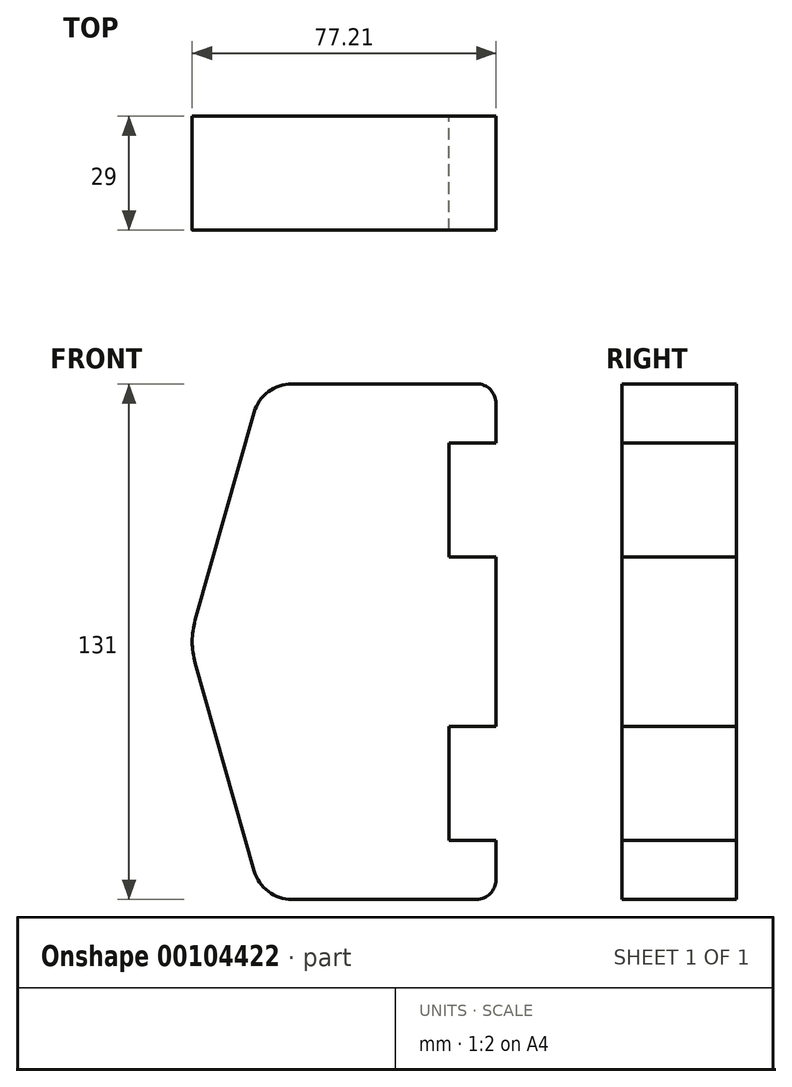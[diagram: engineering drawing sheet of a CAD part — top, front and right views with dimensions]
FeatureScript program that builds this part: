
annotation { "Feature Type Name" : "Feature", "Feature Type Description" : "" }
export const myFeature = defineFeature(function(context is Context, id is Id, definition is map)
    precondition{}
    {
        {
            var Q0;
            Q0=qCreatedBy(makeId("Front.planeOp"),FACE);
            var sketch = newSketch(context, id + "F0", { "sketchPlane" : qUnion([Q0])});
            skLineSegment(sketch, "E0", {"start": v(0, 0) * mm, "end": v(0, 21.5) * mm});
            skLineSegment(sketch, "E1", {"start": v(0, 21.5) * mm, "end": v(-12, 21.5) * mm});
            skLineSegment(sketch, "E2", {"start": v(-12, 21.5) * mm, "end": v(-12, 50.5) * mm});
            skLineSegment(sketch, "E3", {"start": v(-12, 50.5) * mm, "end": v(0, 50.5) * mm});
            skLineSegment(sketch, "E4", {"start": v(0, 50.5) * mm, "end": v(0, 60.5) * mm});
            skLineSegment(sketch, "E5", {"start": v(-5, 65.5) * mm, "end": v(-51.84, 65.5) * mm});
            skLineSegment(sketch, "E6", {"start": v(-61.46, 58.23) * mm, "end": v(-76.45, 5.46) * mm});
            skLineSegment(sketch, "E7", {"start": v(36.06, 0) * mm, "end": v(-91.54, 0) * mm, "construction": true});
            skLineSegment(sketch, "E8.MirrorCS", {"start": v(-61.46, -58.23) * mm, "end": v(-76.45, -5.46) * mm});
            skLineSegment(sketch, "E9.MirrorCS", {"start": v(-5, -65.5) * mm, "end": v(-51.84, -65.5) * mm});
            skLineSegment(sketch, "E10.MirrorCS", {"start": v(0, -50.5) * mm, "end": v(0, -60.5) * mm});
            skLineSegment(sketch, "E11.MirrorCS", {"start": v(-12, -50.5) * mm, "end": v(0, -50.5) * mm});
            skLineSegment(sketch, "E12.MirrorCS", {"start": v(-12, -21.5) * mm, "end": v(-12, -50.5) * mm});
            skLineSegment(sketch, "E13.MirrorCS", {"start": v(0, -21.5) * mm, "end": v(-12, -21.5) * mm});
            skLineSegment(sketch, "E14.MirrorCS", {"start": v(0, 0) * mm, "end": v(0, -21.5) * mm});
            skPoint(sketch, "E15.visualSharp", {"position": v(-59.4, 65.5) * mm});
            skArc(sketch, "E15.filletArc", {"start": v(-51.84, 65.5) * mm, "mid": v(-57.87, 63.48) * mm, "end": v(-61.46, 58.23) * mm});
            skPoint(sketch, "E16.visualSharp", {"position": v(0, 65.5) * mm});
            skArc(sketch, "E16.filletArc", {"start": v(0, 60.5) * mm, "mid": v(-1.46, 64.04) * mm, "end": v(-5, 65.5) * mm});
            skPoint(sketch, "E17.visualSharp", {"position": v(-78, 0) * mm});
            skArc(sketch, "E17.filletArc", {"start": v(-76.45, 5.46) * mm, "mid": v(-77.2, 0) * mm, "end": v(-76.45, -5.46) * mm});
            skPoint(sketch, "E18.visualSharp", {"position": v(-59.4, -65.5) * mm});
            skArc(sketch, "E18.filletArc", {"start": v(-61.46, -58.23) * mm, "mid": v(-57.87, -63.48) * mm, "end": v(-51.84, -65.5) * mm});
            skPoint(sketch, "E19.visualSharp", {"position": v(0, -65.5) * mm});
            skArc(sketch, "E19.filletArc", {"start": v(-5, -65.5) * mm, "mid": v(-1.46, -64.04) * mm, "end": v(0, -60.5) * mm});
            skSolve(sketch);
        }
        {
            var Q0;
            Q0=makeQuery(id+"F0.imprint","IMPRINT",FACE,{"disambiguationData":[TD([[makeQuery(id+"F0.imprint","IMPRINT",EDGE,{"derivedFrom":sQuery(id+"F0.wireOp",EDGE,"E0")}),1.0]])]});
            extrude(context, id + "F1", {"entities" : qUnion([Q0]), "depth" : 29 * mm, "offsetDistance" : 25 * mm});
        }
    });
